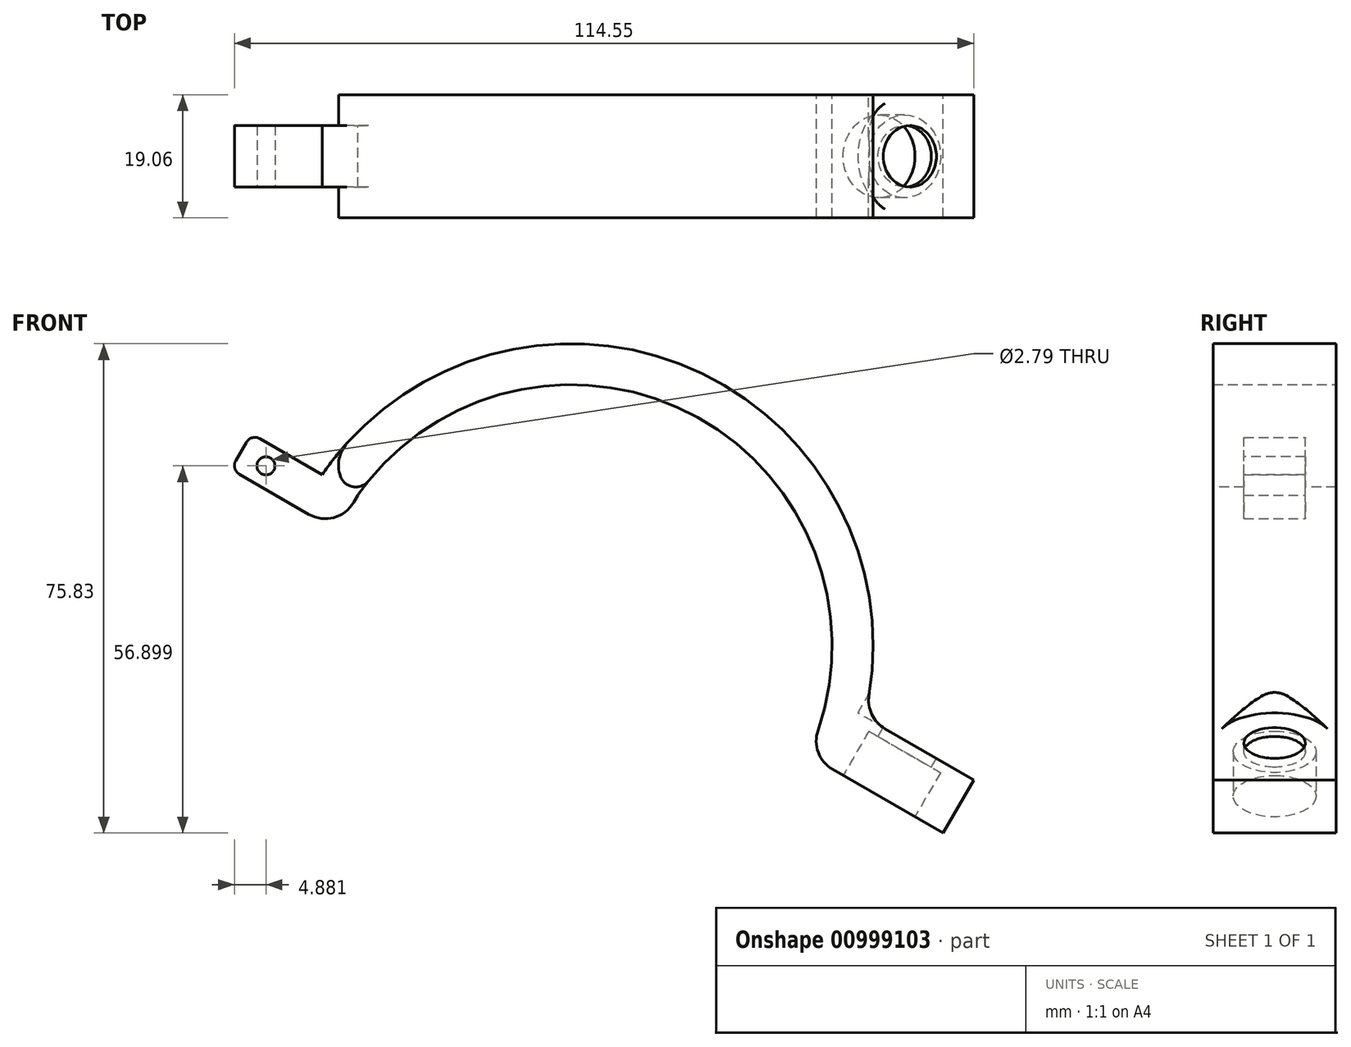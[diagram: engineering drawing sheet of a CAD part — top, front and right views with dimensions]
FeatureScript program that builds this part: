
annotation { "Feature Type Name" : "Feature", "Feature Type Description" : "" }
export const myFeature = defineFeature(function(context is Context, id is Id, definition is map)
    precondition{}
    {
        {
            var Q0;
            Q0=qCreatedBy(makeId("Front.planeOp"),FACE);
            var sketch = newSketch(context, id + "F0", { "sketchPlane" : qUnion([Q0])});
            skArc(sketch, "E0", {"start": v(36.72, -16.97) * mm, "mid": v(20.22, 35.03) * mm, "end": v(-33.05, 23.32) * mm});
            skArc(sketch, "E1", {"start": v(42.24, -20.15) * mm, "mid": v(23.4, 40.53) * mm, "end": v(-38.57, 26.5) * mm});
            skLineSegment(sketch, "E2", {"start": v(-38.57, 26.5) * mm, "end": v(42.24, -20.15) * mm, "construction": true});
            skPoint(sketch, "E3", {"position": v(1.83, 3.18) * mm});
            skLineSegment(sketch, "E4", {"start": v(-38.57, 26.5) * mm, "end": v(-33.05, 23.32) * mm});
            skLineSegment(sketch, "E5", {"start": v(42.24, -20.15) * mm, "end": v(36.72, -16.97) * mm});
            skSolve(sketch);
        }
        {
            var Q0;
            Q0 = qSketchRegion(id + "F0", true);
            extrude(context, id + "F1", {"entities" : qUnion([Q0]), "endBound" : BoundingType.SYMMETRIC, "depth" : 19.05 * mm, "offsetDistance" : 25.4 * mm});
        }
        {
            var Q0;
            Q0=makeQuery(id+"F1.opExtrude","SWEPT_FACE",FACE,{"disambiguationData":[OSD([sQuery(id+"F0.wireOp",EDGE,"E4")])]});
            var sketch = newSketch(context, id + "F2", { "sketchPlane" : qUnion([Q0])});
            skLineSegment(sketch, "E6.bottom", {"start": v(-40.28, -4.76) * mm, "end": v(-59.33, -4.76) * mm});
            skLineSegment(sketch, "E6.top", {"start": v(-40.28, 4.76) * mm, "end": v(-59.33, 4.76) * mm});
            skLineSegment(sketch, "E6.left", {"start": v(-40.28, -4.76) * mm, "end": v(-40.28, 4.76) * mm});
            skLineSegment(sketch, "E6.right", {"start": v(-59.33, -4.76) * mm, "end": v(-59.33, 4.76) * mm});
            skPoint(sketch, "E6.middle", {"position": v(-49.8, 0) * mm});
            skSolve(sketch);
        }
        {
            var Q0;
            Q0 = qSketchRegion(id + "F2", true);
            extrude(context, id + "F3", {"entities" : qUnion([Q0]), "operationType" : NewBodyOperationType.ADD, "depth" : 6.35 * mm, "offsetDistance" : 25.4 * mm});
        }
        {
            var Q0;
            Q0=makeQuery(id+"F1.opExtrude","SWEPT_FACE",FACE,{"disambiguationData":[OSD([sQuery(id+"F0.wireOp",EDGE,"E5")])]});
            var sketch = newSketch(context, id + "F4", { "sketchPlane" : qUnion([Q0])});
            skLineSegment(sketch, "E7.bottom", {"start": v(40.28, 9.53) * mm, "end": v(64.41, 9.53) * mm});
            skLineSegment(sketch, "E7.top", {"start": v(40.28, -9.53) * mm, "end": v(64.41, -9.53) * mm});
            skLineSegment(sketch, "E7.left", {"start": v(40.28, 9.53) * mm, "end": v(40.28, -9.53) * mm});
            skLineSegment(sketch, "E7.right", {"start": v(64.41, 9.53) * mm, "end": v(64.41, -9.52) * mm});
            skSolve(sketch);
        }
        {
            var Q0;
            Q0 = qSketchRegion(id + "F4", true);
            extrude(context, id + "F5", {"entities" : qUnion([Q0]), "operationType" : NewBodyOperationType.ADD, "oppositeDirection" : true, "depth" : 9.52 * mm, "offsetDistance" : 25.4 * mm});
        }
        {
            var Q0;
            Q0=makeQuery(id+"F3.opExtrude","SWEPT_FACE",FACE,{"disambiguationData":[OSD([sQuery(id+"F2.wireOp",EDGE,"E6.top")])]});
            var sketch = newSketch(context, id + "F6", { "sketchPlane" : qUnion([Q0])});
            skPoint(sketch, "E8", {"position": v(-47.29, 27.87) * mm});
            skLineSegment(sketch, "E9", {"start": v(-51.14, 30.1) * mm, "end": v(-47.29, 27.87) * mm});
            skSolve(sketch);
        }
        {
            var Q0;
            Q0=sQuery(id+"F6.wireOp",VERTEX,"E8");
            var Q1;
            Q1=makeQuery(id+"F1.opExtrude","SWEPT_BODY",BODY,{"disambiguationData":[OSD([sQuery(id+"F0.wireOp",EDGE,"E0"),sQuery(id+"F0.wireOp",EDGE,"E1"),sQuery(id+"F0.wireOp",EDGE,"E4"),sQuery(id+"F0.wireOp",EDGE,"E5")])]});
            hole(context, id + "F7", {"style" : HoleStyle.SIMPLE, "endStyle" : HoleEndStyle.THROUGH, "standardTappedOrClearance" : lookupTablePath({ "standard" : "ANSI", "size" : "#35 (0.1)", "type" : "Drilled" }), "standardBlindInLast" : lookupTablePath({ "standard" : "ANSI", "size" : "#35 (0.1)", "type" : "Drilled" }), "holeDiameter" : 2.8 * mm, "majorDiameter" : 6.35 * mm, "isTappedThrough" : true, "tappedDepth" : 12.7 * mm, "tapClearance" : 3, "locations" : qUnion([Q0]), "scope" : qUnion([Q1])});
        }
        {
            var Q0;
            Q0=makeQuery(id+"F5.opExtrude","CAP_FACE",FACE,{"disambiguationData":[OSD([sQuery(id+"F4.wireOp",EDGE,"E7.bottom"),sQuery(id+"F4.wireOp",EDGE,"E7.top"),sQuery(id+"F4.wireOp",EDGE,"E7.left"),sQuery(id+"F4.wireOp",EDGE,"E7.right")])],"isStart":false});
            var sketch = newSketch(context, id + "F8", { "sketchPlane" : qUnion([Q0])});
            skCircle(sketch, "E10", {"center": v(52.98, 0) * mm, "radius": 3.18 * mm});
            skLineSegment(sketch, "E11", {"start": v(64.41, 0) * mm, "end": v(52.98, 0) * mm});
            skSolve(sketch);
        }
        {
            var Q0;
            Q0 = qSketchRegion(id + "F8", true);
            extrude(context, id + "F9", {"entities" : qUnion([Q0]), "operationType" : NewBodyOperationType.REMOVE, "oppositeDirection" : true, "depth" : 25.4 * mm, "offsetDistance" : 25.4 * mm});
        }
        {
            var Q0;
            Q0=makeQuery(id+"F5.opExtrude","CAP_FACE",FACE,{"disambiguationData":[OSD([sQuery(id+"F4.wireOp",EDGE,"E7.bottom"),sQuery(id+"F4.wireOp",EDGE,"E7.top"),sQuery(id+"F4.wireOp",EDGE,"E7.left"),sQuery(id+"F4.wireOp",EDGE,"E7.right")])],"isStart":false});
            var sketch = newSketch(context, id + "F10", { "sketchPlane" : qUnion([Q0])});
            skCircle(sketch, "E12", {"center": v(52.98, 0) * mm, "radius": 4.76 * mm});
            skSolve(sketch);
        }
        {
            var Q0;
            Q0 = qSketchRegion(id + "F10", true);
            extrude(context, id + "F11", {"entities" : qUnion([Q0]), "operationType" : NewBodyOperationType.REMOVE, "oppositeDirection" : true, "depth" : 2.54 * mm, "offsetDistance" : 25.4 * mm});
        }
        {
            var Q0;
            Q0=makeQuery(id+"F5.boolean.opBoolean","INTERSECT",EDGE,{"derivedFrom":[makeQuery(id+"F1.opExtrude","SWEPT_FACE",FACE,{"disambiguationData":[OSD([sQuery(id+"F0.wireOp",EDGE,"E1")])]}),makeQuery(id+"F5.opExtrude","CAP_FACE",FACE,{"disambiguationData":[OSD([sQuery(id+"F4.wireOp",EDGE,"E7.bottom"),sQuery(id+"F4.wireOp",EDGE,"E7.top"),sQuery(id+"F4.wireOp",EDGE,"E7.left"),sQuery(id+"F4.wireOp",EDGE,"E7.right")])],"isStart":false})]});
            var Q1;
            {var subQ0=sQuery(id+"F0.wireOp",EDGE,"E1");Q1=makeQuery(id+"F3.boolean.opBoolean","SPLIT",EDGE,{"disambiguationData":[topologyDisambiguationEdgeConnected([makeQuery(id+"F1.opExtrude","SWEPT_FACE",FACE,{"disambiguationData":[OSD([subQ0])]}),makeQuery(id+"F3.opExtrude","CAP_FACE",FACE,{"disambiguationData":[OSD([sQuery(id+"F2.wireOp",EDGE,"E6.bottom"),sQuery(id+"F2.wireOp",EDGE,"E6.top"),sQuery(id+"F2.wireOp",EDGE,"E6.left"),sQuery(id+"F2.wireOp",EDGE,"E6.right")])],"isStart":true})])],"derivedFrom":makeQuery(id+"F1.opExtrude","SWEPT_EDGE",EDGE,{"disambiguationData":[OSD([subQ0,sQuery(id+"F0.wireOp",EDGE,"E4")])]})});}
            var Q2;
            Q2=makeQuery(id+"F3.opExtrude","CAP_EDGE",EDGE,{"disambiguationData":[OSD([sQuery(id+"F2.wireOp",EDGE,"E6.left")])],"isStart":false});
            var Q3;
            Q3=makeQuery(id+"F1.opExtrude","SWEPT_EDGE",EDGE,{"disambiguationData":[OSD([sQuery(id+"F0.wireOp",EDGE,"E0"),sQuery(id+"F0.wireOp",EDGE,"E5")])]});
            fillet(context, id + "F12", {"entities" : qUnion([Q0, Q1, Q2, Q3]), "radius" : 5.08 * mm, "tangentPropagation" : true, "allowEdgeOverflow" : false});
        }
        {
            var Q0;
            Q0=makeQuery(id+"F3.opExtrude","CAP_EDGE",EDGE,{"disambiguationData":[OSD([sQuery(id+"F2.wireOp",EDGE,"E6.right")])],"isStart":true});
            var Q1;
            Q1=makeQuery(id+"F3.opExtrude","CAP_EDGE",EDGE,{"disambiguationData":[OSD([sQuery(id+"F2.wireOp",EDGE,"E6.right")])],"isStart":false});
            fillet(context, id + "F13", {"entities" : qUnion([Q0, Q1]), "radius" : 1.52 * mm, "tangentPropagation" : true, "allowEdgeOverflow" : false});
        }
        {
            var Q0;
            {var subQ0=sQuery(id+"F2.wireOp",EDGE,"E6.top");var subQ1=sQuery(id+"F0.wireOp",EDGE,"E4");var subQ2=sQuery(id+"F0.wireOp",EDGE,"E1");var subQ3=makeQuery(id+"F1.opExtrude","SWEPT_FACE",FACE,{"disambiguationData":[OSD([subQ1])]});var subQ4=makeQuery(id+"F1.opExtrude","SWEPT_FACE",FACE,{"disambiguationData":[OSD([subQ2])]});Q0=makeQuery(id+"F3.boolean.opBoolean","SPLIT",EDGE,{"disambiguationData":[topologyDisambiguationEdgeConnected([subQ4,subQ3]),TD([makeQuery(id+"F3.opExtrude","SWEPT_FACE",FACE,{"disambiguationData":[OSD([subQ0])]})])],"derivedFrom":makeQuery(id+"F1.opExtrude","SWEPT_EDGE",EDGE,{"disambiguationData":[OSD([subQ2,subQ1])]})});}
            var Q1;
            {var subQ0=sQuery(id+"F0.wireOp",EDGE,"E4");var subQ1=sQuery(id+"F0.wireOp",EDGE,"E0");Q1=makeQuery(id+"F3.boolean.opBoolean","SPLIT",EDGE,{"disambiguationData":[TD([makeQuery(id+"F3.opExtrude","SWEPT_FACE",FACE,{"disambiguationData":[OSD([sQuery(id+"F2.wireOp",EDGE,"E6.top")])]})])],"derivedFrom":makeQuery(id+"F1.opExtrude","SWEPT_EDGE",EDGE,{"disambiguationData":[OSD([subQ1,subQ0])]})});}
            var Q2;
            {var subQ0=sQuery(id+"F0.wireOp",EDGE,"E4");var subQ1=makeQuery(id+"F1.opExtrude","SWEPT_FACE",FACE,{"disambiguationData":[OSD([subQ0])]});var subQ2=sQuery(id+"F2.wireOp",EDGE,"E6.bottom");var subQ3=sQuery(id+"F0.wireOp",EDGE,"E1");var subQ4=makeQuery(id+"F1.opExtrude","SWEPT_FACE",FACE,{"disambiguationData":[OSD([subQ3])]});Q2=makeQuery(id+"F3.boolean.opBoolean","SPLIT",EDGE,{"disambiguationData":[topologyDisambiguationEdgeConnected([subQ4,subQ1]),TD([makeQuery(id+"F3.opExtrude","SWEPT_FACE",FACE,{"disambiguationData":[OSD([subQ2])]})])],"derivedFrom":makeQuery(id+"F1.opExtrude","SWEPT_EDGE",EDGE,{"disambiguationData":[OSD([subQ3,subQ0])]})});}
            var Q3;
            {var subQ0=sQuery(id+"F0.wireOp",EDGE,"E4");var subQ1=sQuery(id+"F0.wireOp",EDGE,"E0");Q3=makeQuery(id+"F3.boolean.opBoolean","SPLIT",EDGE,{"disambiguationData":[TD([makeQuery(id+"F3.opExtrude","SWEPT_FACE",FACE,{"disambiguationData":[OSD([sQuery(id+"F2.wireOp",EDGE,"E6.bottom")])]})])],"derivedFrom":makeQuery(id+"F1.opExtrude","SWEPT_EDGE",EDGE,{"disambiguationData":[OSD([subQ1,subQ0])]})});}
            fillet(context, id + "F14", {"entities" : qUnion([Q0, Q1, Q2, Q3]), "radius" : 2.54 * mm, "tangentPropagation" : true, "allowEdgeOverflow" : false});
        }
        {
            var Q0;
            Q0=makeQuery(id+"F5.boolean.opBoolean","MERGE",FACE,{"derivedFrom":[makeQuery(id+"F1.opExtrude","SWEPT_FACE",FACE,{"disambiguationData":[OSD([sQuery(id+"F0.wireOp",EDGE,"E5")])]}),makeQuery(id+"F5.opExtrude","CAP_FACE",FACE,{"disambiguationData":[OSD([sQuery(id+"F4.wireOp",EDGE,"E7.bottom"),sQuery(id+"F4.wireOp",EDGE,"E7.top"),sQuery(id+"F4.wireOp",EDGE,"E7.left"),sQuery(id+"F4.wireOp",EDGE,"E7.right")])],"isStart":true})]});
            var sketch = newSketch(context, id + "F15", { "sketchPlane" : qUnion([Q0])});
            skCircle(sketch, "E13", {"center": v(52.98, 0) * mm, "radius": 6.42 * mm});
            skCircle(sketch, "E14.cCircle", {"center": v(52.98, 0) * mm, "radius": 6.42 * mm, "construction": true});
            skLineSegment(sketch, "E14.0", {"start": v(53.23, 6.41) * mm, "end": v(58.66, 2.99) * mm, "construction": true});
            skLineSegment(sketch, "E14.1", {"start": v(58.66, 2.99) * mm, "end": v(58.41, -3.42) * mm, "construction": true});
            skLineSegment(sketch, "E14.2", {"start": v(58.41, -3.42) * mm, "end": v(52.73, -6.41) * mm, "construction": true});
            skLineSegment(sketch, "E14.3", {"start": v(52.73, -6.41) * mm, "end": v(47.3, -2.99) * mm, "construction": true});
            skLineSegment(sketch, "E14.4", {"start": v(47.3, -2.99) * mm, "end": v(47.56, 3.42) * mm, "construction": true});
            skLineSegment(sketch, "E14.5", {"start": v(47.56, 3.42) * mm, "end": v(53.23, 6.41) * mm, "construction": true});
            skSolve(sketch);
        }
        {
            var Q0;
            Q0 = qSketchRegion(id + "F15", true);
            extrude(context, id + "F16", {"entities" : qUnion([Q0]), "operationType" : NewBodyOperationType.REMOVE, "oppositeDirection" : true, "depth" : 7.94 * mm, "offsetDistance" : 25.4 * mm});
        }
        {
            var Q0;
            Q0=makeQuery(id+"F5.opExtrude","CAP_FACE",FACE,{"disambiguationData":[OSD([sQuery(id+"F4.wireOp",EDGE,"E7.bottom"),sQuery(id+"F4.wireOp",EDGE,"E7.top"),sQuery(id+"F4.wireOp",EDGE,"E7.left"),sQuery(id+"F4.wireOp",EDGE,"E7.right")])],"isStart":false});
            var sketch = newSketch(context, id + "F17", { "sketchPlane" : qUnion([Q0])});
            skCircle(sketch, "E15", {"center": v(52.98, 0) * mm, "radius": 9.32 * mm});
            skSolve(sketch);
        }
        {
            var Q0;
            Q0 = qSketchRegion(id + "F17", true);
            extrude(context, id + "F18", {"entities" : qUnion([Q0]), "operationType" : NewBodyOperationType.REMOVE, "depth" : 25.4 * mm, "offsetDistance" : 25.4 * mm});
        }
    });
